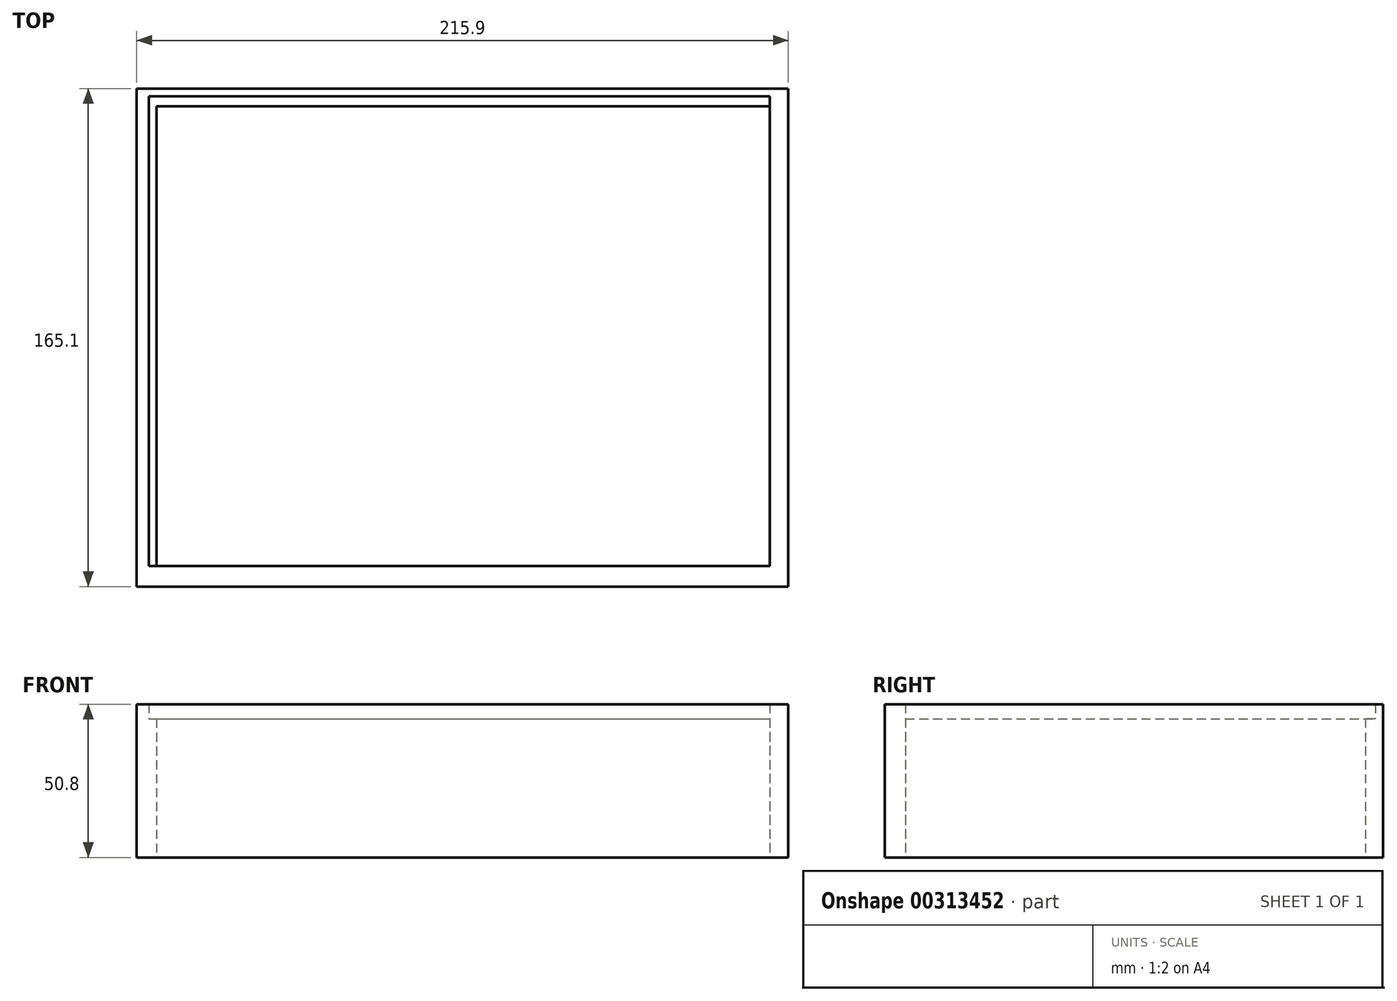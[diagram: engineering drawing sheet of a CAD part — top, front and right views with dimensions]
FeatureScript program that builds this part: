
annotation { "Feature Type Name" : "Feature", "Feature Type Description" : "" }
export const myFeature = defineFeature(function(context is Context, id is Id, definition is map)
    precondition{}
    {
        {
            var Q0;
            Q0=qCreatedBy(makeId("Top.planeOp"),FACE);
            var sketch = newSketch(context, id + "F0", { "sketchPlane" : qUnion([Q0])});
            skLineSegment(sketch, "E0.bottom", {"start": v(0, 0) * mm, "end": v(215.9, 0) * mm});
            skLineSegment(sketch, "E0.top", {"start": v(0, 165.1) * mm, "end": v(215.9, 165.1) * mm});
            skLineSegment(sketch, "E0.left", {"start": v(0, 0) * mm, "end": v(0, 165.1) * mm});
            skLineSegment(sketch, "E0.right", {"start": v(215.9, 0) * mm, "end": v(215.9, 165.1) * mm});
            skSolve(sketch);
        }
        {
            var Q0;
            Q0=makeQuery(id+"F0.imprint","IMPRINT",FACE,{"disambiguationData":[TD([[makeQuery(id+"F0.imprint","IMPRINT",EDGE,{"derivedFrom":sQuery(id+"F0.wireOp",EDGE,"E0.bottom")}),1.0]])]});
            extrude(context, id + "F1", {"entities" : qUnion([Q0]), "depth" : 50.8 * mm});
        }
        {
            var Q0;
            Q0=makeQuery(id+"F1.opExtrude","CAP_FACE",FACE,{"disambiguationData":[OSD([sQuery(id+"F0.wireOp",EDGE,"E0.bottom"),sQuery(id+"F0.wireOp",EDGE,"E0.top"),sQuery(id+"F0.wireOp",EDGE,"E0.left"),sQuery(id+"F0.wireOp",EDGE,"E0.right")])],"isStart":true});
            var sketch = newSketch(context, id + "F2", { "sketchPlane" : qUnion([Q0])});
            skLineSegment(sketch, "E1.bottom", {"start": v(6.54, -6.8) * mm, "end": v(209.74, -6.8) * mm});
            skLineSegment(sketch, "E1.top", {"start": v(6.54, -159.2) * mm, "end": v(209.74, -159.2) * mm});
            skLineSegment(sketch, "E1.left", {"start": v(6.54, -6.8) * mm, "end": v(6.54, -159.2) * mm});
            skLineSegment(sketch, "E1.right", {"start": v(209.74, -6.8) * mm, "end": v(209.74, -159.2) * mm});
            skSolve(sketch);
        }
        {
            var Q0;
            Q0=makeQuery(id+"F2.imprint","IMPRINT",FACE,{"disambiguationData":[TD([[makeQuery(id+"F2.imprint","IMPRINT",EDGE,{"derivedFrom":sQuery(id+"F2.wireOp",EDGE,"E1.bottom")}),-1.0]])]});
            extrude(context, id + "F3", {"entities" : qUnion([Q0]), "operationType" : NewBodyOperationType.REMOVE, "oppositeDirection" : true, "depth" : 50.8 * mm});
        }
        {
            var Q0;
            Q0=makeQuery(id+"F3.boolean.opBoolean","COPY",FACE,{"derivedFrom":makeQuery(id+"F3.opExtrude","SWEPT_FACE",FACE,{"disambiguationData":[OSD([sQuery(id+"F2.wireOp",EDGE,"E1.left")])]})});
            var sketch = newSketch(context, id + "F4", { "sketchPlane" : qUnion([Q0])});
            skLineSegment(sketch, "E2.bottom", {"start": v(6.8, 50.8) * mm, "end": v(159.2, 50.8) * mm});
            skLineSegment(sketch, "E2.top", {"start": v(6.8, 45.96) * mm, "end": v(159.2, 45.96) * mm});
            skLineSegment(sketch, "E2.left", {"start": v(6.8, 50.8) * mm, "end": v(6.8, 45.96) * mm});
            skLineSegment(sketch, "E2.right", {"start": v(159.2, 50.8) * mm, "end": v(159.2, 45.96) * mm});
            skSolve(sketch);
        }
        {
            var Q0;
            Q0=makeQuery(id+"F4.imprint","IMPRINT",FACE,{"disambiguationData":[TD([[makeQuery(id+"F4.imprint","IMPRINT",EDGE,{"derivedFrom":sQuery(id+"F4.wireOp",EDGE,"E2.bottom")}),-1.0]])]});
            extrude(context, id + "F5", {"entities" : qUnion([Q0]), "operationType" : NewBodyOperationType.REMOVE, "oppositeDirection" : true, "depth" : 2.54 * mm});
        }
        {
            var Q0;
            Q0=makeQuery(id+"F5.boolean.opBoolean","MERGE",FACE,{"derivedFrom":[makeQuery(id+"F3.boolean.opBoolean","COPY",FACE,{"derivedFrom":makeQuery(id+"F3.opExtrude","SWEPT_FACE",FACE,{"disambiguationData":[OSD([sQuery(id+"F2.wireOp",EDGE,"E1.top")])]})}),makeQuery(id+"F5.opExtrude","SWEPT_FACE",FACE,{"disambiguationData":[OSD([sQuery(id+"F4.wireOp",EDGE,"E2.right")])]})]});
            var sketch = newSketch(context, id + "F6", { "sketchPlane" : qUnion([Q0])});
            skLineSegment(sketch, "E3.bottom", {"start": v(4, 45.96) * mm, "end": v(209.74, 45.96) * mm});
            skLineSegment(sketch, "E3.top", {"start": v(4, 50.8) * mm, "end": v(209.74, 50.8) * mm});
            skLineSegment(sketch, "E3.left", {"start": v(4, 45.96) * mm, "end": v(4, 50.8) * mm});
            skLineSegment(sketch, "E3.right", {"start": v(209.74, 45.96) * mm, "end": v(209.74, 50.8) * mm});
            skSolve(sketch);
        }
        {
            var Q0;
            Q0 = qSketchRegion(id + "F6", true);
            extrude(context, id + "F7", {"entities" : qUnion([Q0]), "operationType" : NewBodyOperationType.REMOVE, "oppositeDirection" : true, "depth" : 3.3 * mm});
        }
    });
